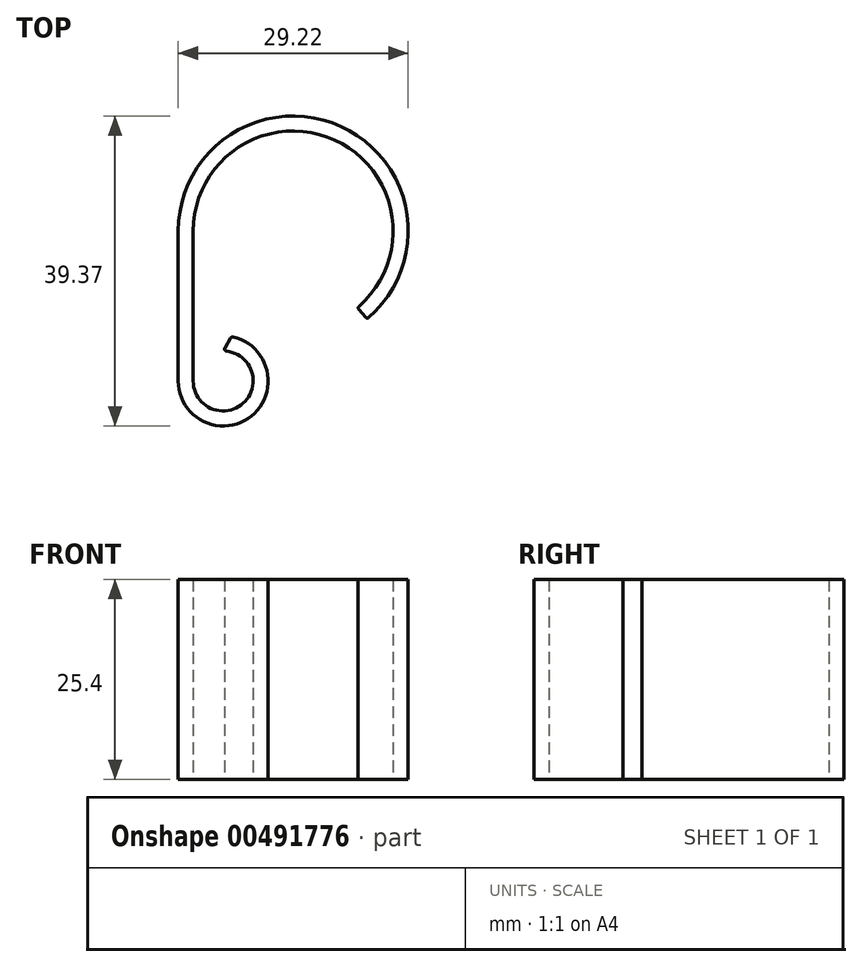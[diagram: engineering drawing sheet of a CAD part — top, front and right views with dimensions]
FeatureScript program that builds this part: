
annotation { "Feature Type Name" : "Feature", "Feature Type Description" : "" }
export const myFeature = defineFeature(function(context is Context, id is Id, definition is map)
    precondition{}
    {
        {
            var Q0;
            Q0=qCreatedBy(makeId("Top.planeOp"),FACE);
            var sketch = newSketch(context, id + "F0", { "sketchPlane" : qUnion([Q0])});
            skCircle(sketch, "E0", {"center": v(0, 0) * mm, "radius": 12.7 * mm, "construction": true});
            skCircle(sketch, "E1", {"center": v(-8.89, -19.05) * mm, "radius": 3.81 * mm, "construction": true});
            skLineSegment(sketch, "E2", {"start": v(-12.7, 0) * mm, "end": v(-12.7, -19.05) * mm});
            skArc(sketch, "E3", {"start": v(-12.7, 0) * mm, "mid": v(5.37, 11.51) * mm, "end": v(8.16, -9.73) * mm});
            skArc(sketch, "E4", {"start": v(-12.7, -19.05) * mm, "mid": v(-6.2, -21.74) * mm, "end": v(-8.89, -15.24) * mm});
            skLineSegment(sketch, "E5", {"start": v(0, 0) * mm, "end": v(8.16, -9.73) * mm, "construction": true});
            skArc(sketch, "E6.0", {"start": v(-14.6, 0) * mm, "mid": v(6.17, 13.24) * mm, "end": v(9.39, -11.19) * mm});
            skLineSegment(sketch, "E6.1", {"start": v(-14.6, 0) * mm, "end": v(-14.6, -19.05) * mm});
            skArc(sketch, "E6.2", {"start": v(-14.6, -19.05) * mm, "mid": v(-5.24, -23.44) * mm, "end": v(-7.85, -13.43) * mm});
            skLineSegment(sketch, "E7", {"start": v(-7.85, -13.43) * mm, "end": v(-8.89, -15.24) * mm});
            skLineSegment(sketch, "E8", {"start": v(8.16, -9.73) * mm, "end": v(9.39, -11.19) * mm});
            skSolve(sketch);
        }
        {
            var Q0;
            Q0=makeQuery(id+"F0.imprint","IMPRINT",FACE,{"disambiguationData":[TD([[makeQuery(id+"F0.imprint","IMPRINT",EDGE,{"derivedFrom":sQuery(id+"F0.wireOp",EDGE,"E2")}),-1.0]])]});
            extrude(context, id + "F1", {"entities" : qUnion([Q0]), "depth" : 25.4 * mm});
        }
        {
            var Q0;
            Q0=makeQuery(id+"F1.opExtrude","SWEPT_EDGE",EDGE,{"disambiguationData":[OSD([sQuery(id+"F0.wireOp",EDGE,"E3"),sQuery(id+"F0.wireOp",EDGE,"E8")])]});
            var Q1;
            Q1=makeQuery(id+"F1.opExtrude","SWEPT_EDGE",EDGE,{"disambiguationData":[OSD([sQuery(id+"F0.wireOp",EDGE,"E6.0"),sQuery(id+"F0.wireOp",EDGE,"E8")])]});
            var Q2;
            Q2=makeQuery(id+"F1.opExtrude","SWEPT_EDGE",EDGE,{"disambiguationData":[OSD([sQuery(id+"F0.wireOp",EDGE,"E6.2"),sQuery(id+"F0.wireOp",EDGE,"E7")])]});
            var Q3;
            Q3=makeQuery(id+"F1.opExtrude","SWEPT_EDGE",EDGE,{"disambiguationData":[OSD([sQuery(id+"F0.wireOp",EDGE,"E4"),sQuery(id+"F0.wireOp",EDGE,"E7")])]});
            fillet(context, id + "F2", {"entities" : qUnion([Q0, Q1, Q2, Q3]), "radius" : 0.25 * mm, "tangentPropagation" : true, "allowEdgeOverflow" : false});
        }
    });
